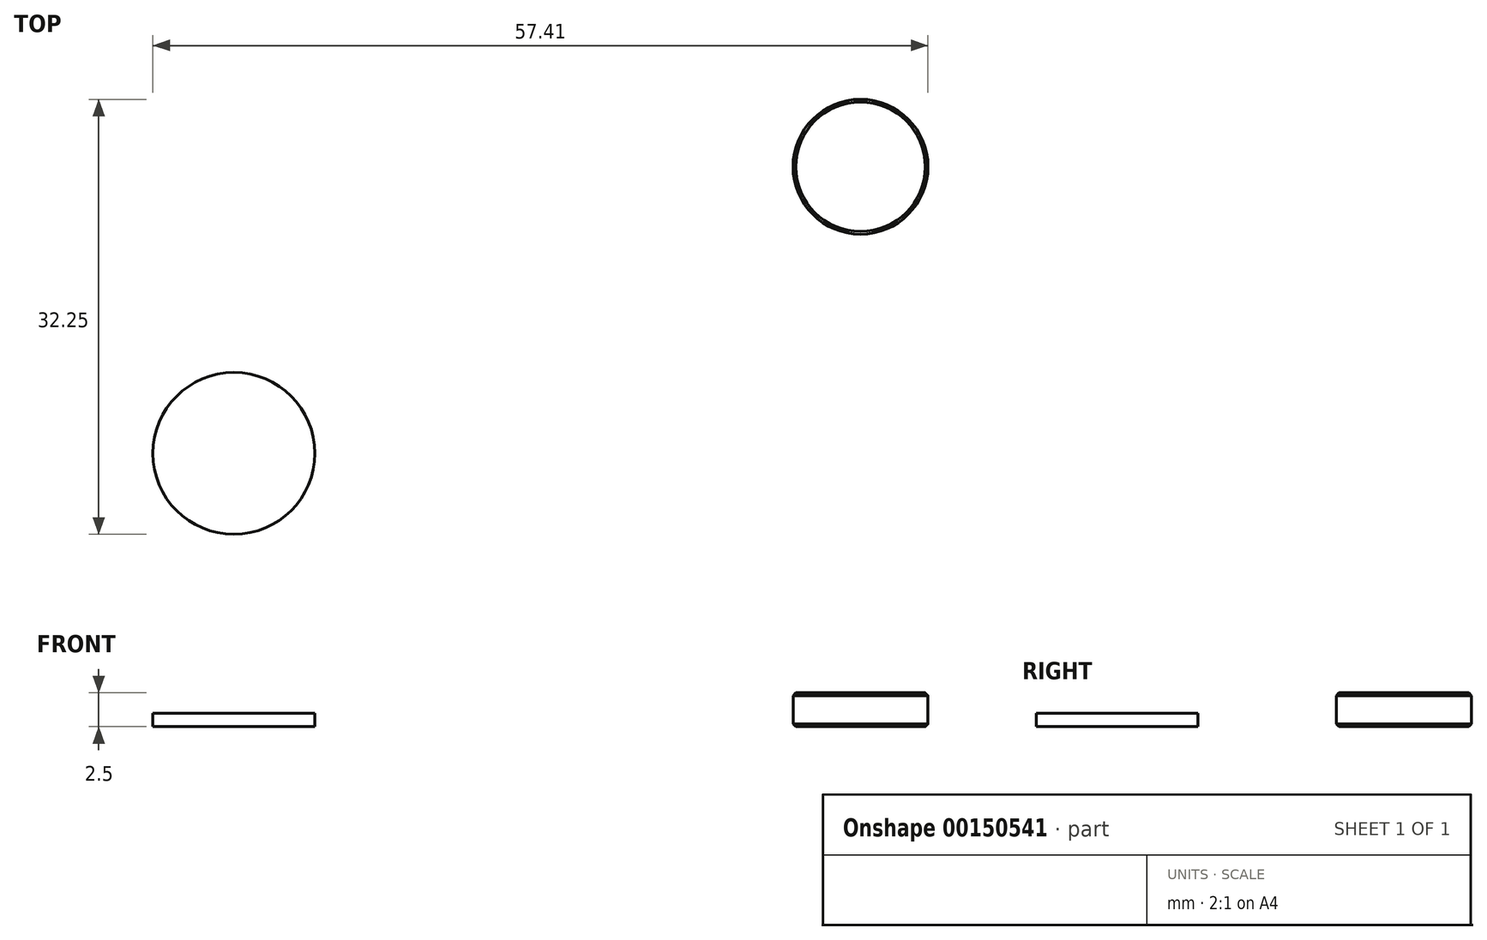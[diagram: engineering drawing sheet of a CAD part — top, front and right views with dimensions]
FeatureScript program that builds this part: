
annotation { "Feature Type Name" : "Feature", "Feature Type Description" : "" }
export const myFeature = defineFeature(function(context is Context, id is Id, definition is map)
    precondition{}
    {
        {
            var Q0;
            Q0=qCreatedBy(makeId("Top.planeOp"),FACE);
            var sketch = newSketch(context, id + "F0", { "sketchPlane" : qUnion([Q0])});
            skCircle(sketch, "E0", {"center": v(0, 0) * mm, "radius": 5 * mm});
            skSolve(sketch);
        }
        {
            var Q0;
            Q0=makeQuery(id+"F0.imprint","IMPRINT",FACE,{"disambiguationData":[TD([[makeQuery(id+"F0.imprint","IMPRINT",EDGE,{"derivedFrom":sQuery(id+"F0.wireOp",EDGE,"E0")}),1.0]])]});
            extrude(context, id + "F1", {"entities" : qUnion([Q0]), "depth" : 2.5 * mm});
        }
        {
            var Q0;
            Q0=makeQuery(id+"F1.opExtrude","CAP_EDGE",EDGE,{"disambiguationData":[OSD([sQuery(id+"F0.wireOp",EDGE,"E0")])],"isStart":false});
            var Q1;
            Q1=makeQuery(id+"F1.opExtrude","CAP_EDGE",EDGE,{"disambiguationData":[OSD([sQuery(id+"F0.wireOp",EDGE,"E0")])],"isStart":true});
            chamfer(context, id + "F2", {"entities" : qUnion([Q0, Q1]), "width" : 0.2 * mm, "tangentPropagation" : true});
        }
        {
            var Q0;
            Q0=qCreatedBy(makeId("Top.planeOp"),FACE);
            var sketch = newSketch(context, id + "F3", { "sketchPlane" : qUnion([Q0])});
            skCircle(sketch, "E1", {"center": v(-46.41, -21.25) * mm, "radius": 6 * mm});
            skSolve(sketch);
        }
        {
            var Q0;
            Q0=makeQuery(id+"F3.imprint","IMPRINT",FACE,{"disambiguationData":[TD([[makeQuery(id+"F3.imprint","IMPRINT",EDGE,{"derivedFrom":sQuery(id+"F3.wireOp",EDGE,"E1")}),1.0]])]});
            extrude(context, id + "F4", {"entities" : qUnion([Q0]), "depth" : 1 * mm});
        }
    });
